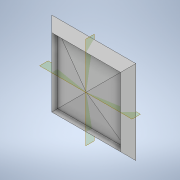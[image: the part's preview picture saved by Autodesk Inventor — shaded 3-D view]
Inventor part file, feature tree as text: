
AUTODESK INVENTOR PART (.ipt)
format: ipt  version: 2021 (Build 250183000, 183)  size: 130,560 bytes
history: native  units: in
note: dims shown in document units (in); Inventor stores cm internally (conversion verified against a paired STEP export)
features: extrude x3, sketch x3, plane x2, projected_geometry x2, chamfer x1
ambient origin geometry x8: Origin, YZ Plane, XZ Plane, XY Plane, X Axis, Y Axis, Z Axis, Center Point
bodies: Solid1 (feature_tree)
feature tree (11):
  extrude  "Extrusion1"  Depth=1.7323in
  chamfer  "Chamfer1"  Distance=0.1575in
  plane  "Work Plane1"
  extrude  "Extrusion4"  Depth=1.4173in TaperAngle=0.0deg
  plane  "Work Plane2"
  extrude  "Extrusion5"  Depth=1.4173in TaperAngle=0.0deg
  sketch  "Sketch1"  dims[d0=1.7323in d1=1.7323in d2=0.1575in d3=0.0in]
  sketch  "Sketch5"  dims[d4=0.1575in d5=0.0787in d6=45.0deg d23=1.4173in d24=0.0in]
  projected_geometry  "Projected Loop4"
  sketch  "Sketch6"  dims[d25=0.0394in d26=1.4173in d27=0.0in]
  projected_geometry  "Projected Loop5"
